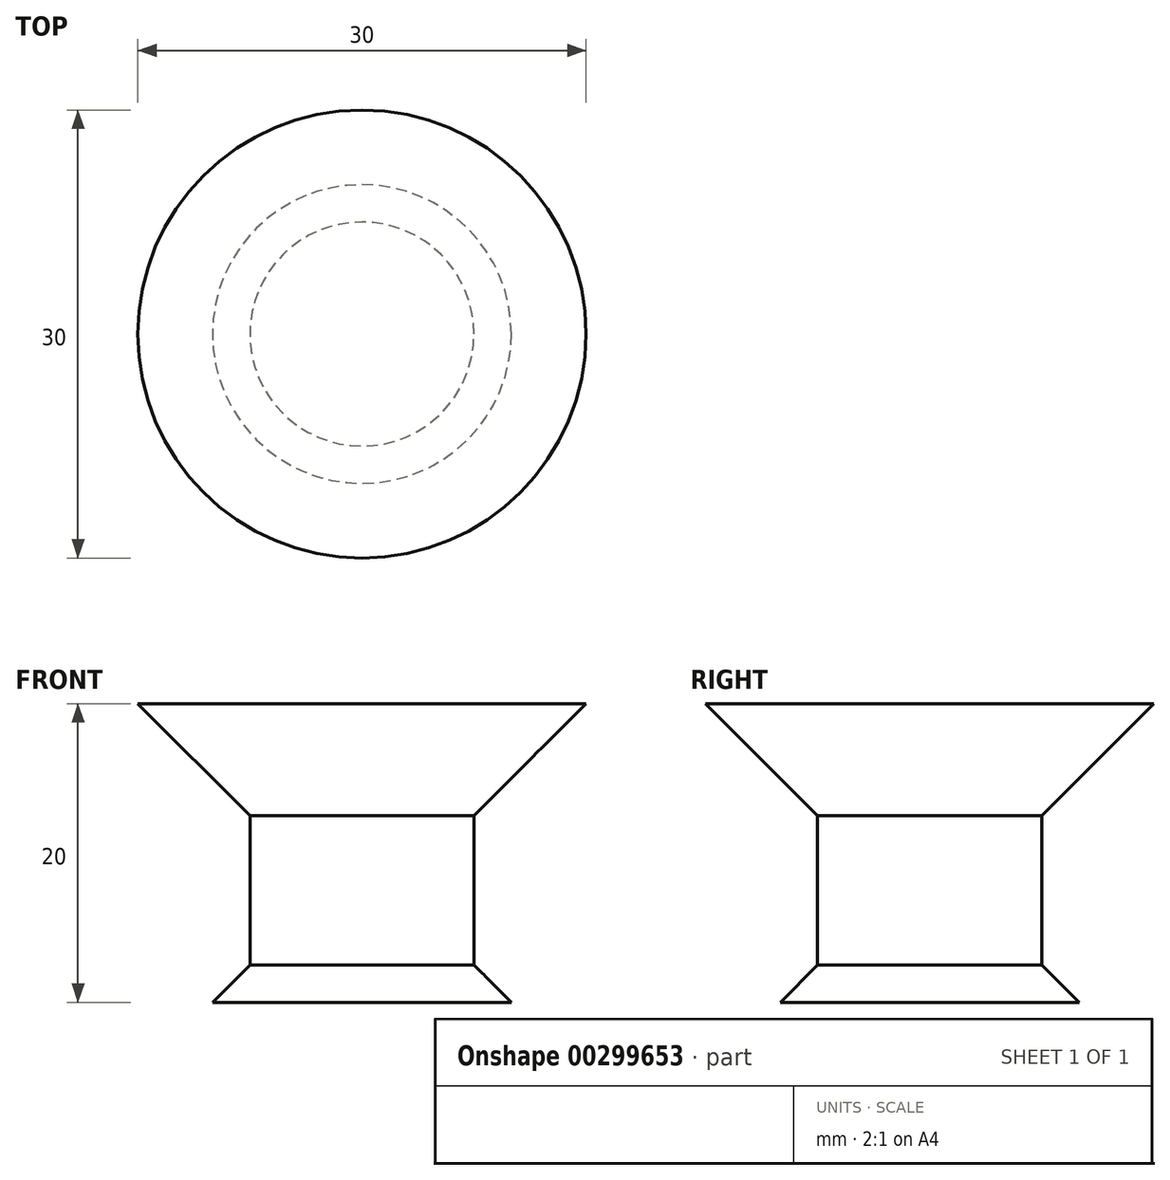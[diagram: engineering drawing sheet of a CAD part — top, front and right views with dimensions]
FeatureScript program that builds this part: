
annotation { "Feature Type Name" : "Feature", "Feature Type Description" : "" }
export const myFeature = defineFeature(function(context is Context, id is Id, definition is map)
    precondition{}
    {
        {
            var Q0;
            Q0=qCreatedBy(makeId("Front.planeOp"),FACE);
            var sketch = newSketch(context, id + "F0", { "sketchPlane" : qUnion([Q0])});
            skLineSegment(sketch, "E0", {"start": v(0, 10.98) * mm, "end": v(15, 10.98) * mm});
            skLineSegment(sketch, "E1", {"start": v(15, 10.98) * mm, "end": v(7.5, 3.48) * mm});
            skLineSegment(sketch, "E2", {"start": v(7.5, 3.48) * mm, "end": v(7.5, -6.52) * mm});
            skLineSegment(sketch, "E3", {"start": v(7.5, -6.52) * mm, "end": v(10, -9.02) * mm});
            skLineSegment(sketch, "E4", {"start": v(10, -9.02) * mm, "end": v(0, -9.02) * mm});
            skLineSegment(sketch, "E5", {"start": v(0, -9.02) * mm, "end": v(0, 10.98) * mm});
            skLineSegment(sketch, "E6", {"start": v(0, 21.99) * mm, "end": v(0, -20.4) * mm, "construction": true});
            skSolve(sketch);
        }
        {
            var Q0;
            Q0=makeQuery(id+"F0.imprint","IMPRINT",FACE,{"disambiguationData":[TD([[makeQuery(id+"F0.imprint","IMPRINT",EDGE,{"derivedFrom":sQuery(id+"F0.wireOp",EDGE,"E0")}),-1.0]])]});
            var Q1;
            Q1=sQuery(id+"F0.wireOp",EDGE,"E6");
            revolve(context, id + "F1", {"entities" : qUnion([Q0]), "axis" : qUnion([Q1]), "revolveType" : RevolveType.FULL});
        }
    });
